# Revit family: Medical_Equipment-Workstation-Midmark_Medical-6215-Compact-Kidney_Top-v1
name_source: partatom
category: Specialty Equipment
units: mm (PartAtom-declared; Revit-internal decimal feet)

## family parameters
Always vertical = Yes
Cut with Voids When Loaded = No
OmniClass Number = 23.40.70.11.14.11
OmniClass Title = Medical Equipment
Part Type = Normal
Room Calculation Point = No
Round Connector Dimension = Use Diameter
Shared = No
Work Plane-Based = No

## types (1)
- 6215-003 - Kidney Top
    Assembly Code = E1020800
    Cost = 0 $
    Description = Flat Panel PC Workstation
    Manufacturer = Midmark
    Model = Midmark Medical 6215 Flat Panel PC Workstation
    Product Documentation Link = https://www.midmark.com
    Product Page URL = https://www.midmark.com
    Product data url = https://bimobject.com
    URL = https://www.midmark.com
    Workstation Top Material = Wood - Midmark - Dark Walnut

## geometry (parser evidence)
native form markers: Blend x16, Sweep x27
no freeform markers — native parametric forms only
